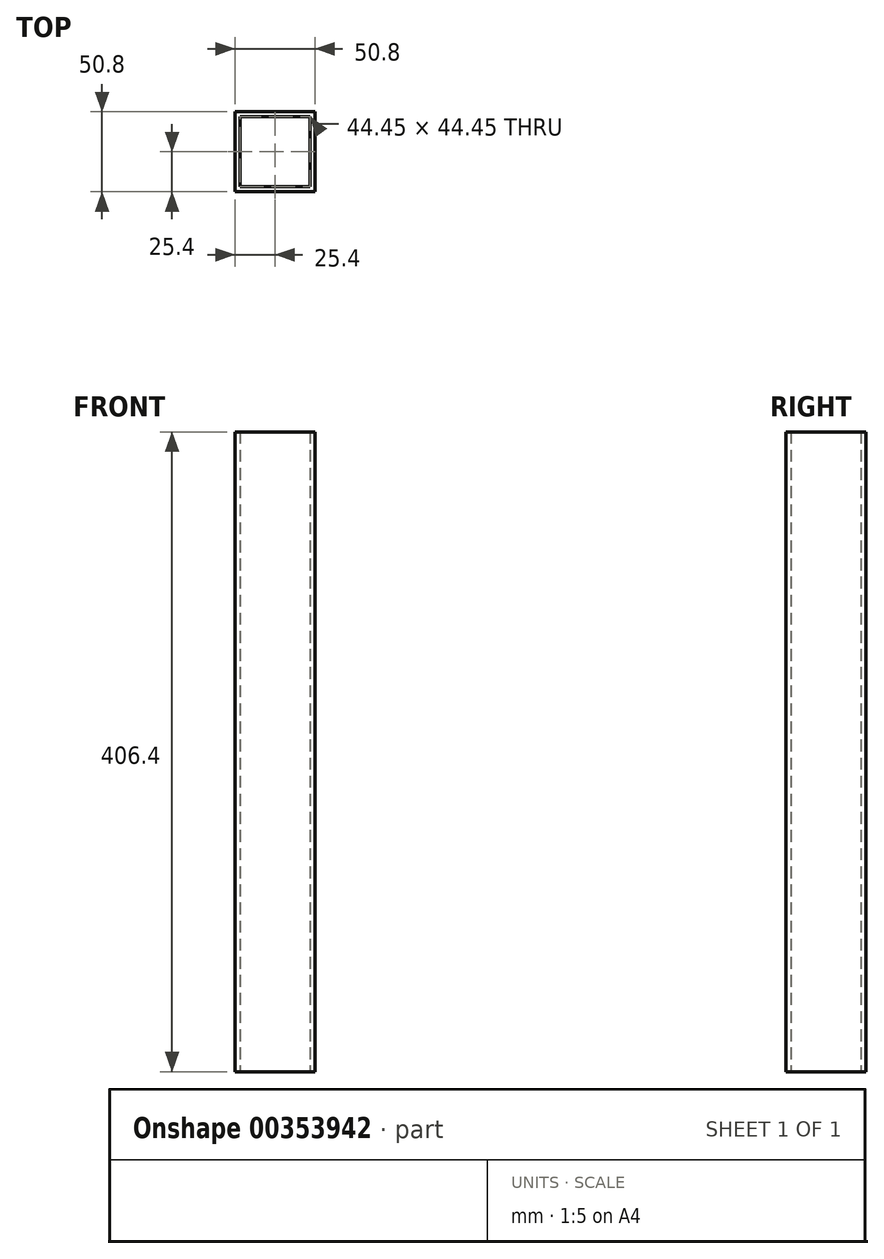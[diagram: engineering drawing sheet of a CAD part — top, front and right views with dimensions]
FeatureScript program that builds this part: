
annotation { "Feature Type Name" : "Feature", "Feature Type Description" : "" }
export const myFeature = defineFeature(function(context is Context, id is Id, definition is map)
    precondition{}
    {
        {
            var Q0;
            Q0=qCreatedBy(makeId("Top.planeOp"),FACE);
            var sketch = newSketch(context, id + "F0", { "sketchPlane" : qUnion([Q0])});
            skLineSegment(sketch, "E0.bottom", {"start": v(25.4, -25.4) * mm, "end": v(-25.4, -25.4) * mm});
            skLineSegment(sketch, "E0.top", {"start": v(25.4, 25.4) * mm, "end": v(-25.4, 25.4) * mm});
            skLineSegment(sketch, "E0.left", {"start": v(25.4, -25.4) * mm, "end": v(25.4, 25.4) * mm});
            skLineSegment(sketch, "E0.right", {"start": v(-25.4, -25.4) * mm, "end": v(-25.4, 25.4) * mm});
            skPoint(sketch, "E0.middle", {"position": v(0, 0) * mm});
            skLineSegment(sketch, "E1.bottom", {"start": v(22.23, -22.23) * mm, "end": v(-22.23, -22.23) * mm});
            skLineSegment(sketch, "E1.top", {"start": v(22.23, 22.23) * mm, "end": v(-22.23, 22.23) * mm});
            skLineSegment(sketch, "E1.left", {"start": v(22.23, -22.23) * mm, "end": v(22.23, 22.23) * mm});
            skLineSegment(sketch, "E1.right", {"start": v(-22.23, -22.23) * mm, "end": v(-22.23, 22.23) * mm});
            skSolve(sketch);
        }
        {
            var Q0;
            Q0 = qSketchRegion(id + "F0", true);
            extrude(context, id + "F1", {"entities" : qUnion([Q0]), "depth" : 406.4 * mm});
        }
    });
